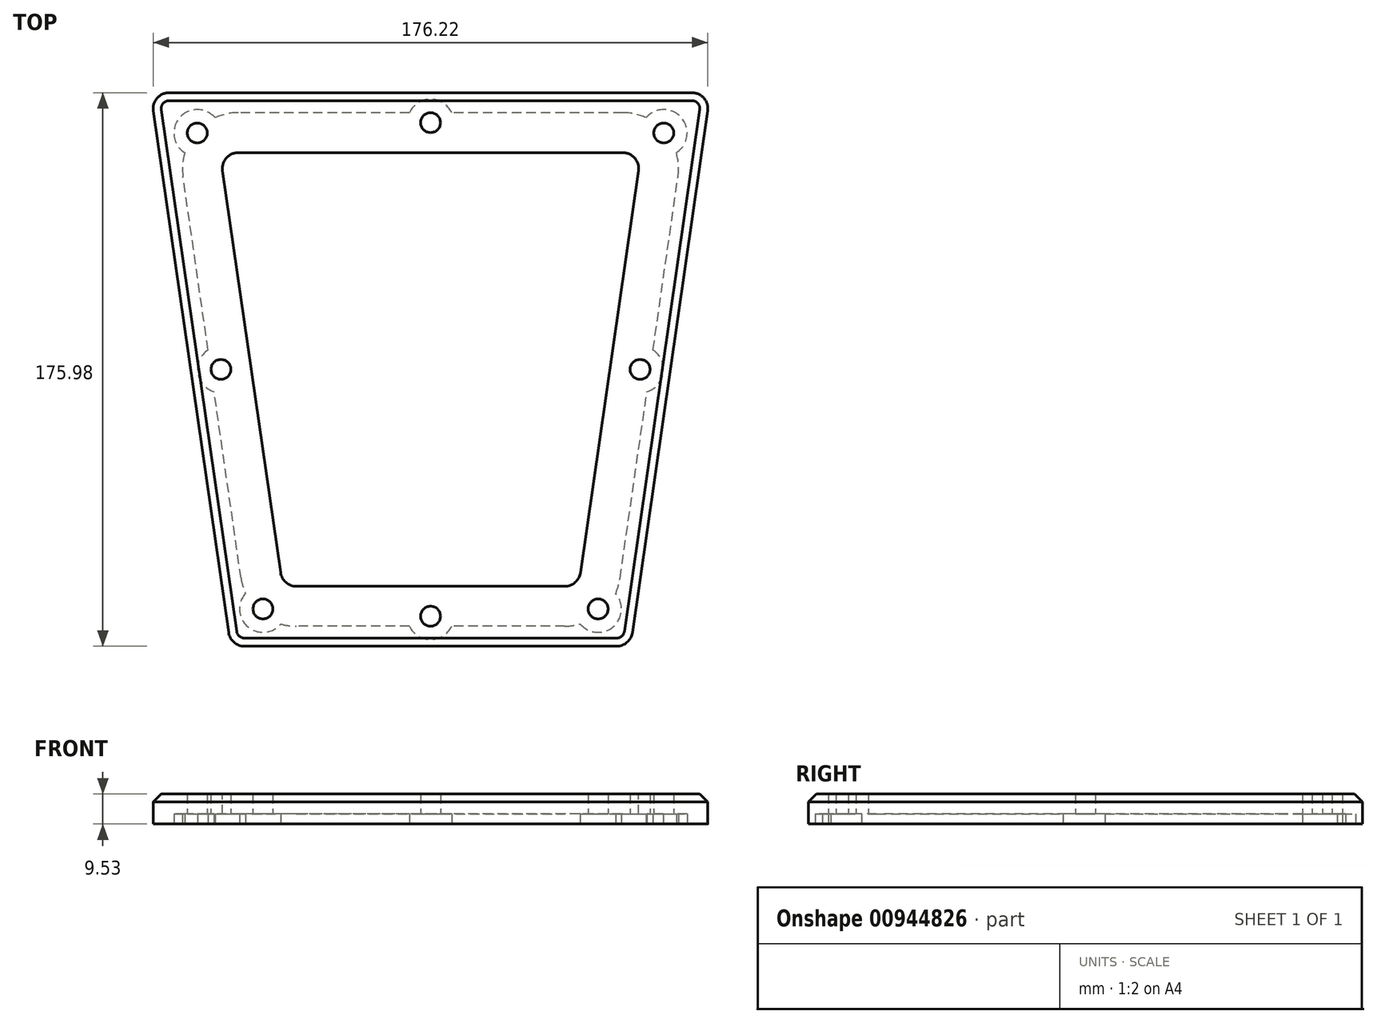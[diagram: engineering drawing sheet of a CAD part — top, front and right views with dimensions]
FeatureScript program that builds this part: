
annotation { "Feature Type Name" : "Feature", "Feature Type Description" : "" }
export const myFeature = defineFeature(function(context is Context, id is Id, definition is map)
    precondition{}
    {
        {
            var Q0;
            Q0=qCreatedBy(makeId("Top.planeOp"),FACE);
            var sketch = newSketch(context, id + "F0", { "sketchPlane" : qUnion([Q0])});
            skLineSegment(sketch, "E0.bottom", {"start": v(-152.4, 175.98) * mm, "end": v(25.4, 175.98) * mm});
            skLineSegment(sketch, "E0.top", {"start": v(-127, 0) * mm, "end": v(0, 0) * mm});
            skLineSegment(sketch, "E0.left", {"start": v(-152.4, 175.98) * mm, "end": v(-127, 0) * mm});
            skLineSegment(sketch, "E0.right", {"start": v(25.4, 175.98) * mm, "end": v(0, 0) * mm});
            skLineSegment(sketch, "E1", {"start": v(-130.4, 156.93) * mm, "end": v(3.4, 156.93) * mm});
            skLineSegment(sketch, "E2", {"start": v(3.4, 156.93) * mm, "end": v(-16.5, 19.05) * mm});
            skLineSegment(sketch, "E3", {"start": v(-16.5, 19.05) * mm, "end": v(-110.5, 19.05) * mm});
            skLineSegment(sketch, "E4", {"start": v(-110.5, 19.05) * mm, "end": v(-130.4, 156.93) * mm});
            skCircle(sketch, "E5", {"center": v(-137.6, 163.16) * mm, "radius": 3.18 * mm});
            skCircle(sketch, "E6", {"center": v(10.6, 163.16) * mm, "radius": 3.18 * mm});
            skCircle(sketch, "E7", {"center": v(-130.08, 87.99) * mm, "radius": 3.18 * mm});
            skCircle(sketch, "E8", {"center": v(3.08, 87.99) * mm, "radius": 3.18 * mm});
            skPoint(sketch, "E8.centerSnap0", {"position": v(-6.55, 87.99) * mm});
            skCircle(sketch, "E9", {"center": v(-116.74, 11.85) * mm, "radius": 3.18 * mm});
            skCircle(sketch, "E10", {"center": v(-10.26, 11.85) * mm, "radius": 3.18 * mm});
            skLineSegment(sketch, "E11", {"start": v(12.7, 87.99) * mm, "end": v(-6.55, 87.99) * mm, "construction": true});
            skLineSegment(sketch, "E12", {"start": v(-120.45, 87.99) * mm, "end": v(-139.7, 87.99) * mm});
            skLineSegment(sketch, "E13", {"start": v(-130.4, 156.93) * mm, "end": v(-152.4, 175.98) * mm, "construction": true});
            skLineSegment(sketch, "E14", {"start": v(25.4, 175.98) * mm, "end": v(3.4, 156.93) * mm, "construction": true});
            skLineSegment(sketch, "E15", {"start": v(-110.5, 19.05) * mm, "end": v(-127, 0) * mm, "construction": true});
            skLineSegment(sketch, "E16", {"start": v(-16.5, 19.05) * mm, "end": v(0, 0) * mm, "construction": true});
            skLineSegment(sketch, "E17", {"start": v(-63.5, 19.05) * mm, "end": v(-63.5, 0) * mm, "construction": true});
            skCircle(sketch, "E18", {"center": v(-63.5, 9.53) * mm, "radius": 3.18 * mm});
            skLineSegment(sketch, "E19", {"start": v(-63.5, 175.98) * mm, "end": v(-63.5, 156.93) * mm, "construction": true});
            skCircle(sketch, "E20", {"center": v(-63.5, 166.45) * mm, "radius": 3.18 * mm});
            skSolve(sketch);
        }
        {
            var Q0;
            Q0 = qSketchRegion(id + "F0", true);
            extrude(context, id + "F1", {"entities" : qUnion([Q0]), "depth" : 9.52 * mm, "offsetDistance" : 25.4 * mm});
        }
        {
            var Q0;
            Q0=makeQuery(id+"F1.opExtrude","SWEPT_EDGE",EDGE,{"disambiguationData":[OSD([sQuery(id+"F0.wireOp",EDGE,"E0.bottom"),sQuery(id+"F0.wireOp",EDGE,"E0.left")])]});
            var Q1;
            Q1=makeQuery(id+"F1.opExtrude","SWEPT_EDGE",EDGE,{"disambiguationData":[OSD([sQuery(id+"F0.wireOp",EDGE,"E1"),sQuery(id+"F0.wireOp",EDGE,"E4")])]});
            var Q2;
            Q2=makeQuery(id+"F1.opExtrude","SWEPT_EDGE",EDGE,{"disambiguationData":[OSD([sQuery(id+"F0.wireOp",EDGE,"E0.bottom"),sQuery(id+"F0.wireOp",EDGE,"E0.right")])]});
            var Q3;
            Q3=makeQuery(id+"F1.opExtrude","SWEPT_EDGE",EDGE,{"disambiguationData":[OSD([sQuery(id+"F0.wireOp",EDGE,"E1"),sQuery(id+"F0.wireOp",EDGE,"E2")])]});
            var Q4;
            Q4=makeQuery(id+"F1.opExtrude","SWEPT_EDGE",EDGE,{"disambiguationData":[OSD([sQuery(id+"F0.wireOp",EDGE,"E0.top"),sQuery(id+"F0.wireOp",EDGE,"E0.left")])]});
            var Q5;
            Q5=makeQuery(id+"F1.opExtrude","SWEPT_EDGE",EDGE,{"disambiguationData":[OSD([sQuery(id+"F0.wireOp",EDGE,"E0.top"),sQuery(id+"F0.wireOp",EDGE,"E0.right")])]});
            var Q6;
            Q6=makeQuery(id+"F1.opExtrude","SWEPT_EDGE",EDGE,{"disambiguationData":[OSD([sQuery(id+"F0.wireOp",EDGE,"E2"),sQuery(id+"F0.wireOp",EDGE,"E3")])]});
            var Q7;
            Q7=makeQuery(id+"F1.opExtrude","SWEPT_EDGE",EDGE,{"disambiguationData":[OSD([sQuery(id+"F0.wireOp",EDGE,"E3"),sQuery(id+"F0.wireOp",EDGE,"E4")])]});
            fillet(context, id + "F2", {"entities" : qUnion([Q0, Q1, Q2, Q3, Q4, Q5, Q6, Q7]), "radius" : 5.08 * mm, "tangentPropagation" : true, "allowEdgeOverflow" : false});
        }
        {
            var Q0;
            Q0=makeQuery(id+"F1.opExtrude","CAP_EDGE",EDGE,{"disambiguationData":[OSD([sQuery(id+"F0.wireOp",EDGE,"E0.top")])],"isStart":false});
            chamfer(context, id + "F3", {"entities" : qUnion([Q0]), "width" : 2.54 * mm, "tangentPropagation" : true});
        }
        {
            var Q0;
            Q0=makeQuery(id+"F1.opExtrude","CAP_FACE",FACE,{"disambiguationData":[OSD([sQuery(id+"F0.wireOp",EDGE,"E0.bottom"),sQuery(id+"F0.wireOp",EDGE,"E0.top"),sQuery(id+"F0.wireOp",EDGE,"E0.left"),sQuery(id+"F0.wireOp",EDGE,"E0.right"),sQuery(id+"F0.wireOp",EDGE,"E1"),sQuery(id+"F0.wireOp",EDGE,"E2"),sQuery(id+"F0.wireOp",EDGE,"E3"),sQuery(id+"F0.wireOp",EDGE,"E4"),sQuery(id+"F0.wireOp",EDGE,"E5"),sQuery(id+"F0.wireOp",EDGE,"E6"),sQuery(id+"F0.wireOp",EDGE,"E7"),sQuery(id+"F0.wireOp",EDGE,"E8"),sQuery(id+"F0.wireOp",EDGE,"E9"),sQuery(id+"F0.wireOp",EDGE,"E10"),sQuery(id+"F0.wireOp",EDGE,"E18"),sQuery(id+"F0.wireOp",EDGE,"E20")])],"isStart":true});
            var sketch = newSketch(context, id + "F4", { "sketchPlane" : qUnion([Q0])});
            skLineSegment(sketch, "E21", {"start": v(-20.9, -6.35) * mm, "end": v(-106.1, -6.35) * mm});
            skLineSegment(sketch, "E22", {"start": v(-123.7, -21.6) * mm, "end": v(-142.13, -149.3) * mm});
            skArc(sketch, "E23", {"start": v(-106.1, -6.35) * mm, "mid": v(-117.74, -10.69) * mm, "end": v(-123.7, -21.6) * mm});
            skLineSegment(sketch, "E24", {"start": v(-3.3, -21.59) * mm, "end": v(15.13, -149.3) * mm});
            skArc(sketch, "E25", {"start": v(-3.3, -21.59) * mm, "mid": v(-9.26, -10.69) * mm, "end": v(-20.9, -6.35) * mm});
            skLineSegment(sketch, "E26", {"start": v(-2.46, -169.63) * mm, "end": v(-124.54, -169.63) * mm});
            skArc(sketch, "E27", {"start": v(-142.13, -149.3) * mm, "mid": v(-137.98, -163.49) * mm, "end": v(-124.54, -169.63) * mm});
            skArc(sketch, "E28", {"start": v(-2.46, -169.63) * mm, "mid": v(10.98, -163.49) * mm, "end": v(15.13, -149.3) * mm});
            skSolve(sketch);
        }
        {
            var Q0;
            Q0 = qSketchRegion(id + "F4", true);
            extrude(context, id + "F5", {"entities" : qUnion([Q0]), "operationType" : NewBodyOperationType.REMOVE, "oppositeDirection" : true, "depth" : 3.17 * mm, "offsetDistance" : 25.4 * mm});
        }
        {
            var Q0;
            Q0=makeQuery(id+"F1.opExtrude","CAP_FACE",FACE,{"disambiguationData":[OSD([sQuery(id+"F0.wireOp",EDGE,"E0.bottom"),sQuery(id+"F0.wireOp",EDGE,"E0.top"),sQuery(id+"F0.wireOp",EDGE,"E0.left"),sQuery(id+"F0.wireOp",EDGE,"E0.right"),sQuery(id+"F0.wireOp",EDGE,"E1"),sQuery(id+"F0.wireOp",EDGE,"E2"),sQuery(id+"F0.wireOp",EDGE,"E3"),sQuery(id+"F0.wireOp",EDGE,"E4"),sQuery(id+"F0.wireOp",EDGE,"E5"),sQuery(id+"F0.wireOp",EDGE,"E6"),sQuery(id+"F0.wireOp",EDGE,"E7"),sQuery(id+"F0.wireOp",EDGE,"E8"),sQuery(id+"F0.wireOp",EDGE,"E9"),sQuery(id+"F0.wireOp",EDGE,"E10"),sQuery(id+"F0.wireOp",EDGE,"E18"),sQuery(id+"F0.wireOp",EDGE,"E20")])],"isStart":true});
            var sketch = newSketch(context, id + "F6", { "sketchPlane" : qUnion([Q0])});
            skCircle(sketch, "E29", {"center": v(-116.74, -11.85) * mm, "radius": 7.43 * mm});
            skPoint(sketch, "E29.centerSnap0", {"position": v(-118.82, -9.45) * mm});
            skPoint(sketch, "E29.perimeterSnap0", {"position": v(-118.82, -9.45) * mm});
            skCircle(sketch, "E30", {"center": v(-63.5, -9.53) * mm, "radius": 7.43 * mm});
            skCircle(sketch, "E31", {"center": v(-10.26, -11.85) * mm, "radius": 7.43 * mm});
            skCircle(sketch, "E32", {"center": v(3.08, -87.99) * mm, "radius": 7.43 * mm});
            skCircle(sketch, "E33", {"center": v(-63.5, -166.45) * mm, "radius": 7.43 * mm});
            skCircle(sketch, "E34", {"center": v(-137.6, -163.16) * mm, "radius": 7.43 * mm});
            skCircle(sketch, "E35", {"center": v(10.6, -163.16) * mm, "radius": 7.43 * mm});
            skCircle(sketch, "E36", {"center": v(-130.08, -87.99) * mm, "radius": 7.43 * mm});
            skSolve(sketch);
        }
        {
            var Q0;
            Q0 = qSketchRegion(id + "F6", true);
            var Q1;
            Q1=makeQuery(id+"F5.boolean.opBoolean","COPY",FACE,{"derivedFrom":makeQuery(id+"F5.opExtrude","CAP_FACE",FACE,{"disambiguationData":[OSD([sQuery(id+"F4.wireOp",EDGE,"E21"),sQuery(id+"F4.wireOp",EDGE,"E22"),sQuery(id+"F4.wireOp",EDGE,"E23"),sQuery(id+"F4.wireOp",EDGE,"E24"),sQuery(id+"F4.wireOp",EDGE,"E25"),sQuery(id+"F4.wireOp",EDGE,"E26"),sQuery(id+"F4.wireOp",EDGE,"E27"),sQuery(id+"F4.wireOp",EDGE,"E28")])],"isStart":false})});
            extrude(context, id + "F7", {"entities" : qUnion([Q0]), "operationType" : NewBodyOperationType.REMOVE, "endBound" : BoundingType.UP_TO_SURFACE, "oppositeDirection" : true, "depth" : 25.4 * mm, "endBoundEntityFace" : qUnion([Q1]), "offsetDistance" : 25.4 * mm});
        }
    });
